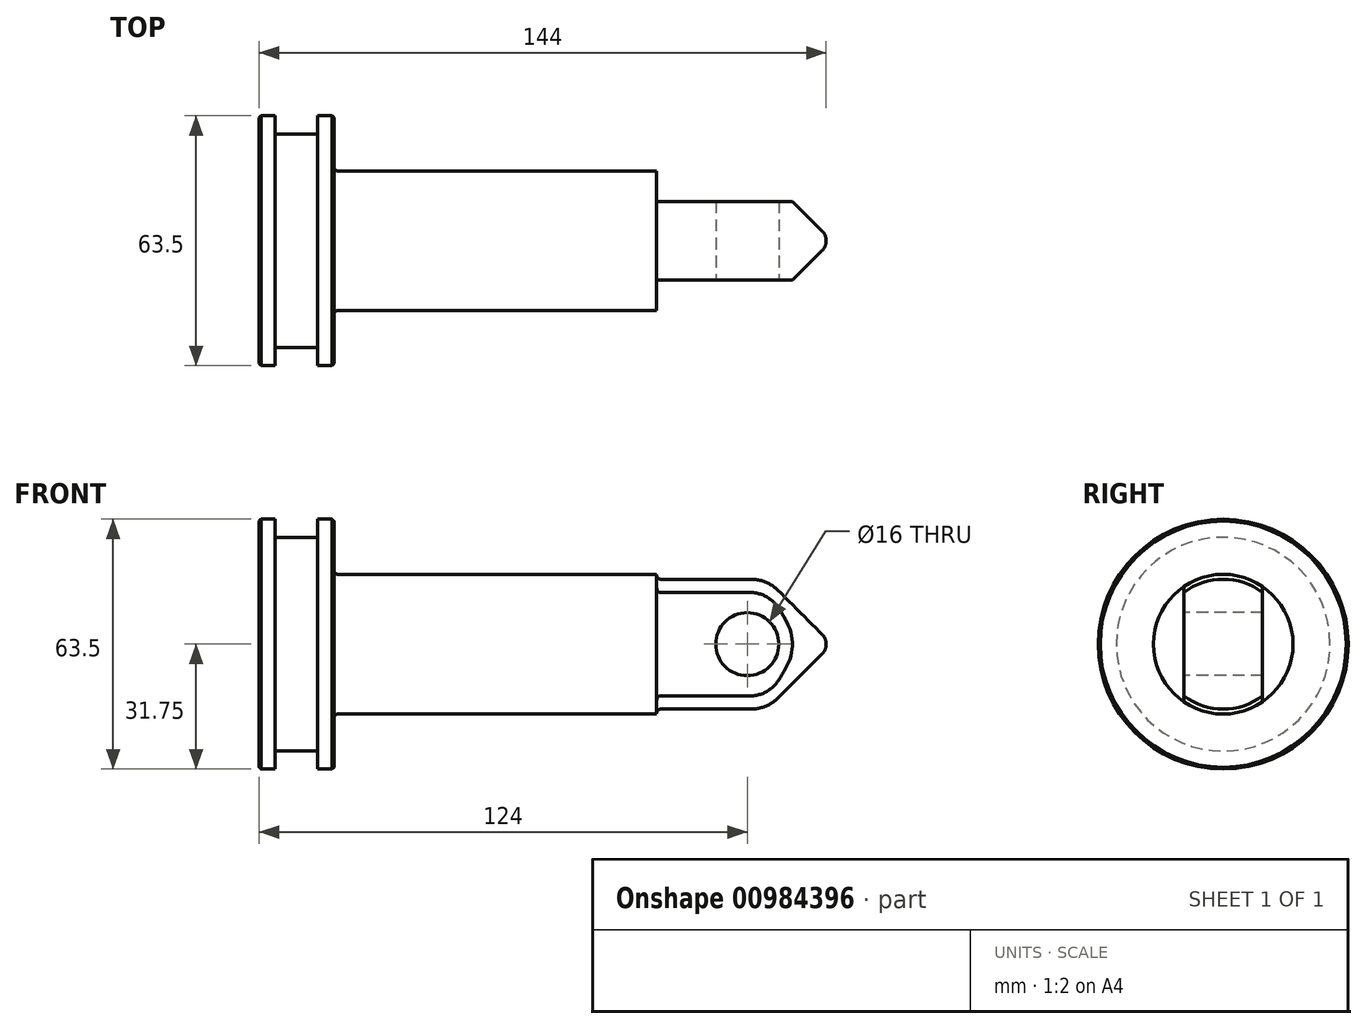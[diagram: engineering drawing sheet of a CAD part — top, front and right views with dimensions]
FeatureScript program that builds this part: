
annotation { "Feature Type Name" : "Feature", "Feature Type Description" : "" }
export const myFeature = defineFeature(function(context is Context, id is Id, definition is map)
    precondition{}
    {
        {
            var Q0;
            Q0=qCreatedBy(makeId("Front.planeOp"),FACE);
            var sketch = newSketch(context, id + "F0", { "sketchPlane" : qUnion([Q0])});
            skLineSegment(sketch, "E0", {"start": v(0, 66.77) * mm, "end": v(0, -65.3) * mm, "construction": true});
            skLineSegment(sketch, "E1", {"start": v(-70.1, 0) * mm, "end": v(69.64, 0) * mm, "construction": true});
            skLineSegment(sketch, "E2", {"start": v(-72, 31.75) * mm, "end": v(-67.9, 31.75) * mm});
            skLineSegment(sketch, "E3", {"start": v(-67.9, 31.75) * mm, "end": v(-67.9, 27.15) * mm});
            skLineSegment(sketch, "E4", {"start": v(-67.9, 27.15) * mm, "end": v(-57.1, 27.15) * mm});
            skLineSegment(sketch, "E5", {"start": v(-57.1, 27.15) * mm, "end": v(-57.1, 31.75) * mm});
            skLineSegment(sketch, "E6", {"start": v(-57.1, 31.75) * mm, "end": v(-53, 31.75) * mm});
            skLineSegment(sketch, "E7", {"start": v(-53, 31.75) * mm, "end": v(-53, 17.75) * mm});
            skLineSegment(sketch, "E8", {"start": v(-53, 17.75) * mm, "end": v(29, 17.75) * mm});
            skLineSegment(sketch, "E9", {"start": v(29, 17.75) * mm, "end": v(29, 16.5) * mm});
            skLineSegment(sketch, "E10", {"start": v(29, 16.5) * mm, "end": v(72, 16.5) * mm});
            skLineSegment(sketch, "E11", {"start": v(72, 16.5) * mm, "end": v(72, 0) * mm});
            skLineSegment(sketch, "E12", {"start": v(72, 0) * mm, "end": v(-72, 0) * mm});
            skLineSegment(sketch, "E13", {"start": v(-72, 0) * mm, "end": v(-72, 31.75) * mm});
            skSolve(sketch);
        }
        {
            var Q0;
            Q0=makeQuery(id+"F0.imprint","IMPRINT",FACE,{"disambiguationData":[TD([[makeQuery(id+"F0.imprint","IMPRINT",EDGE,{"derivedFrom":sQuery(id+"F0.wireOp",EDGE,"E2")}),-1.0]])]});
            var Q1;
            Q1=sQuery(id+"F0.wireOp",EDGE,"E12");
            revolve(context, id + "F1", {"surfaceOperationType" : NewSurfaceOperationType.NEW, "entities" : qUnion([Q0]), "axis" : qUnion([Q1]), "revolveType" : RevolveType.FULL});
        }
        {
            var Q0;
            Q0=makeQuery(id+"F1.opRevolve","SWEPT_FACE",FACE,{"disambiguationData":[OSD([sQuery(id+"F0.wireOp",EDGE,"E11")])]});
            var sketch = newSketch(context, id + "F2", { "sketchPlane" : qUnion([Q0])});
            skLineSegment(sketch, "E14", {"start": v(0, 50.6) * mm, "end": v(0, -55.8) * mm, "construction": true});
            skLineSegment(sketch, "E15", {"start": v(-85.73, 0) * mm, "end": v(83.13, 0) * mm, "construction": true});
            skLineSegment(sketch, "E16", {"start": v(-10, 13.12) * mm, "end": v(-10, -13.12) * mm});
            skLineSegment(sketch, "E17", {"start": v(10, 13.12) * mm, "end": v(10, -13.12) * mm});
            skArc(sketch, "E18", {"start": v(-10, 13.12) * mm, "mid": v(-16.5, 0) * mm, "end": v(-10, -13.12) * mm});
            skArc(sketch, "E19.trimOffspring", {"start": v(10, -13.12) * mm, "mid": v(16.5, 0) * mm, "end": v(10, 13.12) * mm});
            skSolve(sketch);
        }
        {
            var Q0;
            Q0=makeQuery(id+"F2.imprint","IMPRINT",FACE,{"disambiguationData":[TD([[makeQuery(id+"F2.imprint","IMPRINT",EDGE,{"derivedFrom":sQuery(id+"F2.wireOp",EDGE,"E16")}),-1.0]])]});
            var Q1;
            Q1=makeQuery(id+"F2.imprint","IMPRINT",FACE,{"disambiguationData":[TD([[makeQuery(id+"F2.imprint","IMPRINT",EDGE,{"derivedFrom":sQuery(id+"F2.wireOp",EDGE,"E17")}),1.0]])]});
            extrude(context, id + "F3", {"entities" : qUnion([Q0, Q1]), "operationType" : NewBodyOperationType.REMOVE, "oppositeDirection" : true, "depth" : 43 * mm, "offsetDistance" : 25 * mm});
        }
        {
            var Q0;
            Q0=makeQuery(id+"F3.boolean.opBoolean","SPLIT",EDGE,{"disambiguationData":[OD(0.0)],"derivedFrom":makeQuery(id+"F1.opRevolve","SWEPT_EDGE",EDGE,{"disambiguationData":[OSD([sQuery(id+"F0.wireOp",EDGE,"E10"),sQuery(id+"F0.wireOp",EDGE,"E11")])]})});
            chamfer(context, id + "F4", {"entities" : qUnion([Q0]), "chamferType" : ChamferType.OFFSET_ANGLE, "width" : 15 * mm, "oppositeDirection" : false, "angle" : 45 * degree, "tangentPropagation" : true});
        }
        {
            var Q0;
            {var subQ0=sQuery(id+"F0.wireOp",EDGE,"E11");Q0=makeQuery(id+"F4.opChamfer","BLEND_EDGE",EDGE,{"blendedFrom":[makeQuery(id+"F3.boolean.opBoolean","SPLIT",EDGE,{"disambiguationData":[OD(0.0)],"derivedFrom":makeQuery(id+"F1.opRevolve","SWEPT_EDGE",EDGE,{"disambiguationData":[OSD([sQuery(id+"F0.wireOp",EDGE,"E10"),subQ0])]})}),makeQuery(id+"F1.opRevolve","SWEPT_FACE",FACE,{"disambiguationData":[OSD([subQ0])]})],"blendedInto":[makeQuery(id+"F1.opRevolve","SWEPT_FACE",FACE,{"disambiguationData":[OSD([subQ0])]})]});}
            fillet(context, id + "F5", {"entities" : qUnion([Q0]), "radius" : 3 * mm, "tangentPropagation" : true, "allowEdgeOverflow" : false});
        }
        {
            var Q0;
            {var subQ0=sQuery(id+"F0.wireOp",EDGE,"E10");Q0=makeQuery(id+"F4.opChamfer","BLEND_EDGE",EDGE,{"blendedFrom":[makeQuery(id+"F3.boolean.opBoolean","SPLIT",EDGE,{"disambiguationData":[OD(0.0)],"derivedFrom":makeQuery(id+"F1.opRevolve","SWEPT_EDGE",EDGE,{"disambiguationData":[OSD([subQ0,sQuery(id+"F0.wireOp",EDGE,"E11")])]})}),makeQuery(id+"F3.boolean.opBoolean","SPLIT",FACE,{"disambiguationData":[OD(0.0)],"derivedFrom":makeQuery(id+"F1.opRevolve","SWEPT_FACE",FACE,{"disambiguationData":[OSD([subQ0])]})})],"blendedInto":[makeQuery(id+"F3.boolean.opBoolean","SPLIT",FACE,{"disambiguationData":[OD(0.0)],"derivedFrom":makeQuery(id+"F1.opRevolve","SWEPT_FACE",FACE,{"disambiguationData":[OSD([subQ0])]})})]});}
            var Q1;
            {var subQ0=sQuery(id+"F0.wireOp",EDGE,"E10");Q1=makeQuery(id+"F4.opChamfer","BLEND_EDGE",EDGE,{"blendedFrom":[makeQuery(id+"F3.boolean.opBoolean","SPLIT",EDGE,{"disambiguationData":[OD(0.0)],"derivedFrom":makeQuery(id+"F1.opRevolve","SWEPT_EDGE",EDGE,{"disambiguationData":[OSD([subQ0,sQuery(id+"F0.wireOp",EDGE,"E11")])]})}),makeQuery(id+"F3.boolean.opBoolean","SPLIT",FACE,{"disambiguationData":[OD(1.0)],"derivedFrom":makeQuery(id+"F1.opRevolve","SWEPT_FACE",FACE,{"disambiguationData":[OSD([subQ0])]})})],"blendedInto":[makeQuery(id+"F3.boolean.opBoolean","SPLIT",FACE,{"disambiguationData":[OD(1.0)],"derivedFrom":makeQuery(id+"F1.opRevolve","SWEPT_FACE",FACE,{"disambiguationData":[OSD([subQ0])]})})]});}
            fillet(context, id + "F6", {"entities" : qUnion([Q0, Q1]), "radius" : 10 * mm, "tangentPropagation" : true, "allowEdgeOverflow" : false});
        }
        {
            var Q0;
            Q0=makeQuery(id+"F3.boolean.opBoolean","COPY",FACE,{"derivedFrom":makeQuery(id+"F3.opExtrude","SWEPT_FACE",FACE,{"disambiguationData":[OSD([sQuery(id+"F2.wireOp",EDGE,"E16")])]})});
            var sketch = newSketch(context, id + "F7", { "sketchPlane" : qUnion([Q0])});
            skLineSegment(sketch, "E20", {"start": v(102.37, 0) * mm, "end": v(-5.85, 0) * mm, "construction": true});
            skPoint(sketch, "E21", {"position": v(52, 0) * mm});
            skSolve(sketch);
        }
        {
            var Q0;
            Q0=sQuery(id+"F7.wireOp",VERTEX,"E21");
            var Q1;
            Q1=makeQuery(id+"F1.opRevolve","SWEPT_BODY",BODY,{"disambiguationData":[OSD([sQuery(id+"F0.wireOp",EDGE,"E2"),sQuery(id+"F0.wireOp",EDGE,"E3"),sQuery(id+"F0.wireOp",EDGE,"E4"),sQuery(id+"F0.wireOp",EDGE,"E5"),sQuery(id+"F0.wireOp",EDGE,"E6"),sQuery(id+"F0.wireOp",EDGE,"E7"),sQuery(id+"F0.wireOp",EDGE,"E8"),sQuery(id+"F0.wireOp",EDGE,"E9"),sQuery(id+"F0.wireOp",EDGE,"E10"),sQuery(id+"F0.wireOp",EDGE,"E11"),sQuery(id+"F0.wireOp",EDGE,"E12"),sQuery(id+"F0.wireOp",EDGE,"E13")])]});
            hole(context, id + "F8", {"style" : HoleStyle.SIMPLE, "endStyle" : HoleEndStyle.THROUGH, "standardTappedOrClearance" : lookupTablePath({ "standard" : "ISO", "size" : "16", "type" : "Drilled" }), "standardBlindInLast" : lookupTablePath({ "standard" : "ISO", "size" : "16", "type" : "Drilled" }), "holeDiameter" : 16 * mm, "majorDiameter" : 5 * mm, "isTappedThrough" : true, "tappedDepth" : 11.2 * mm, "tapClearance" : 3, "startFromSketch" : true, "locations" : qUnion([Q0]), "scope" : qUnion([Q1])});
        }
        {
            var Q0;
            Q0=makeQuery(id+"F1.opRevolve","SWEPT_EDGE",EDGE,{"disambiguationData":[OSD([sQuery(id+"F0.wireOp",EDGE,"E7"),sQuery(id+"F0.wireOp",EDGE,"E8")])]});
            var Q1;
            Q1=makeQuery(id+"F3.boolean.opBoolean","SPLIT",EDGE,{"disambiguationData":[OD(0.0)],"derivedFrom":makeQuery(id+"F1.opRevolve","SWEPT_EDGE",EDGE,{"disambiguationData":[OSD([sQuery(id+"F0.wireOp",EDGE,"E9"),sQuery(id+"F0.wireOp",EDGE,"E10")])]})});
            var Q2;
            Q2=makeQuery(id+"F3.boolean.opBoolean","SPLIT",EDGE,{"disambiguationData":[OD(1.0)],"derivedFrom":makeQuery(id+"F1.opRevolve","SWEPT_EDGE",EDGE,{"disambiguationData":[OSD([sQuery(id+"F0.wireOp",EDGE,"E9"),sQuery(id+"F0.wireOp",EDGE,"E10")])]})});
            fillet(context, id + "F9", {"entities" : qUnion([Q0, Q1, Q2]), "radius" : 1 * mm, "tangentPropagation" : true, "allowEdgeOverflow" : false});
        }
        {
            var Q0;
            Q0=makeQuery(id+"F1.opRevolve","SWEPT_EDGE",EDGE,{"disambiguationData":[OSD([sQuery(id+"F0.wireOp",EDGE,"E2"),sQuery(id+"F0.wireOp",EDGE,"E13")])]});
            var Q1;
            Q1=makeQuery(id+"F1.opRevolve","SWEPT_EDGE",EDGE,{"disambiguationData":[OSD([sQuery(id+"F0.wireOp",EDGE,"E6"),sQuery(id+"F0.wireOp",EDGE,"E7")])]});
            chamfer(context, id + "F10", {"entities" : qUnion([Q0, Q1]), "width" : 0.5 * mm, "tangentPropagation" : true});
        }
    });
